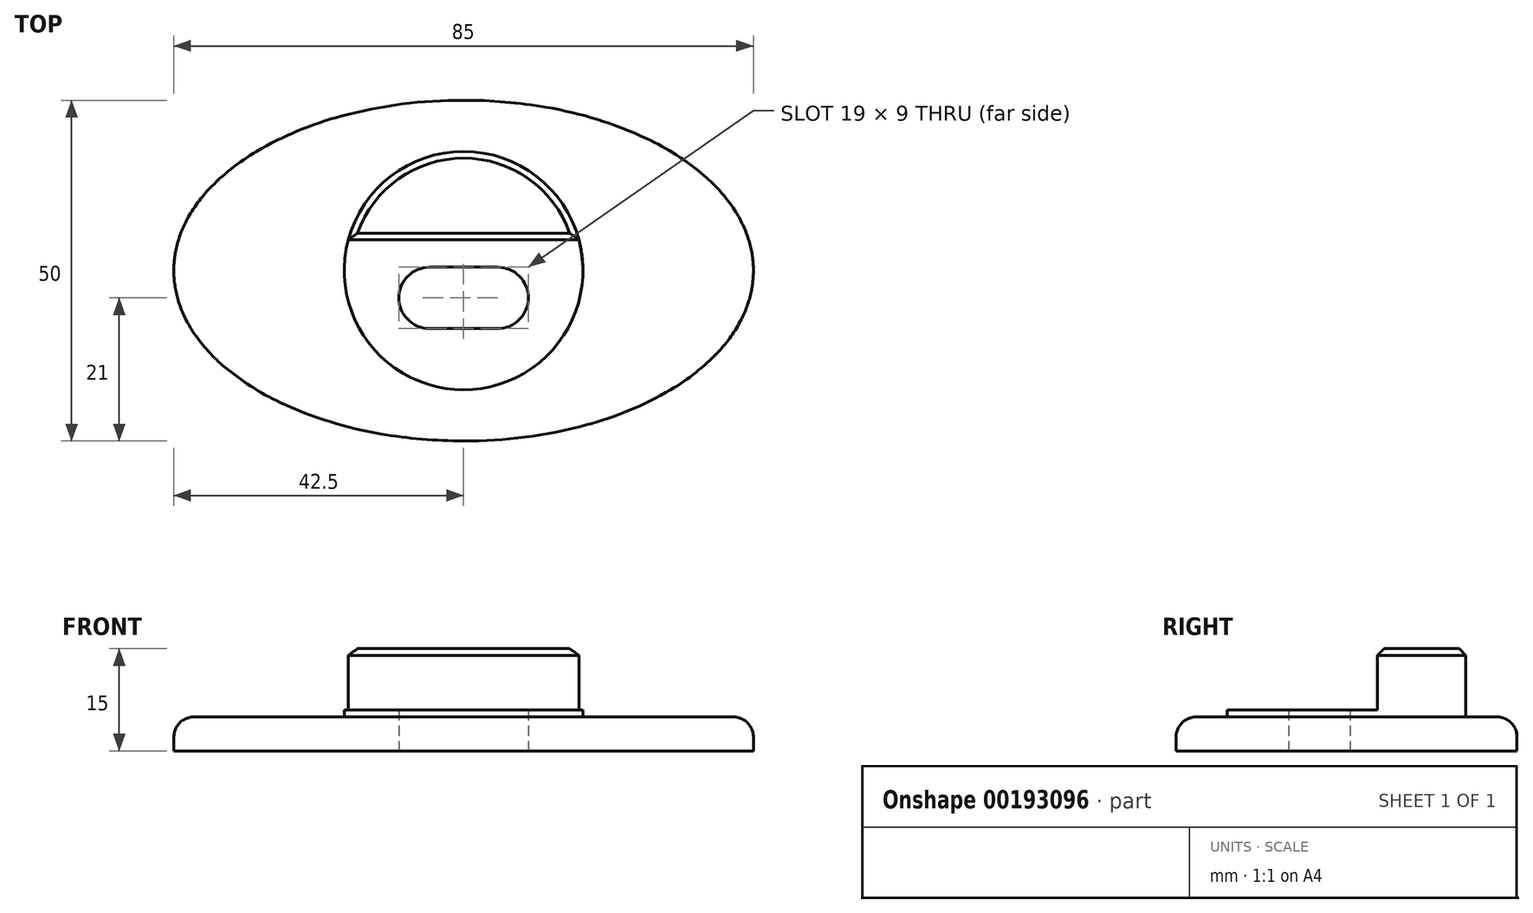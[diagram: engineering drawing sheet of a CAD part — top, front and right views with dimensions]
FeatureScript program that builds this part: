
annotation { "Feature Type Name" : "Feature", "Feature Type Description" : "" }
export const myFeature = defineFeature(function(context is Context, id is Id, definition is map)
    precondition{}
    {
        {
            var Q0;
            Q0=qCreatedBy(makeId("Top.planeOp"),FACE);
            var sketch = newSketch(context, id + "F0", { "sketchPlane" : qUnion([Q0])});
            skArc(sketch, "E0", {"start": v(0, 25) * mm, "mid": v(-9.05, 24.44) * mm, "end": v(-17.95, 22.67) * mm});
            skArc(sketch, "E1", {"start": v(-17.95, 22.67) * mm, "mid": v(-24.33, 20.5) * mm, "end": v(-30.36, 17.5) * mm});
            skArc(sketch, "E2", {"start": v(-30.36, 17.5) * mm, "mid": v(-34.05, 14.96) * mm, "end": v(-37.35, 11.94) * mm});
            skArc(sketch, "E3", {"start": v(-37.35, 11.94) * mm, "mid": v(-39.21, 9.66) * mm, "end": v(-40.74, 7.15) * mm});
            skArc(sketch, "E4", {"start": v(-40.74, 7.15) * mm, "mid": v(-41.66, 4.99) * mm, "end": v(-42.26, 2.72) * mm});
            skArc(sketch, "E5", {"start": v(-42.26, 2.72) * mm, "mid": v(-42.44, 1.37) * mm, "end": v(-42.5, 0) * mm});
            skArc(sketch, "E6", {"start": v(-42.5, 0) * mm, "mid": v(-42.34, -2.18) * mm, "end": v(-41.87, -4.31) * mm});
            skArc(sketch, "E7", {"start": v(-41.87, -4.31) * mm, "mid": v(-40.97, -6.67) * mm, "end": v(-39.75, -8.88) * mm});
            skArc(sketch, "E8", {"start": v(-39.75, -8.88) * mm, "mid": v(-37.7, -11.56) * mm, "end": v(-35.3, -13.92) * mm});
            skArc(sketch, "E9", {"start": v(-35.3, -13.92) * mm, "mid": v(-31.25, -16.94) * mm, "end": v(-26.82, -19.4) * mm});
            skArc(sketch, "E10", {"start": v(-26.82, -19.4) * mm, "mid": v(-19.64, -22.18) * mm, "end": v(-12.15, -23.97) * mm});
            skArc(sketch, "E11", {"start": v(-12.15, -23.97) * mm, "mid": v(-6.1, -24.75) * mm, "end": v(0, -25) * mm});
            skArc(sketch, "E12", {"start": v(0, -25) * mm, "mid": v(9.05, -24.44) * mm, "end": v(17.95, -22.67) * mm});
            skArc(sketch, "E13", {"start": v(17.95, -22.67) * mm, "mid": v(24.33, -20.5) * mm, "end": v(30.36, -17.5) * mm});
            skArc(sketch, "E14", {"start": v(30.36, -17.5) * mm, "mid": v(34.05, -14.96) * mm, "end": v(37.35, -11.94) * mm});
            skArc(sketch, "E15", {"start": v(37.35, -11.94) * mm, "mid": v(39.21, -9.66) * mm, "end": v(40.74, -7.15) * mm});
            skArc(sketch, "E16", {"start": v(40.74, -7.15) * mm, "mid": v(41.66, -4.99) * mm, "end": v(42.26, -2.72) * mm});
            skArc(sketch, "E17", {"start": v(42.26, -2.72) * mm, "mid": v(42.44, -1.37) * mm, "end": v(42.5, 0) * mm});
            skArc(sketch, "E18", {"start": v(42.5, 0) * mm, "mid": v(42.34, 2.18) * mm, "end": v(41.87, 4.31) * mm});
            skArc(sketch, "E19", {"start": v(41.87, 4.31) * mm, "mid": v(40.97, 6.67) * mm, "end": v(39.75, 8.88) * mm});
            skArc(sketch, "E20", {"start": v(39.75, 8.88) * mm, "mid": v(37.7, 11.56) * mm, "end": v(35.3, 13.92) * mm});
            skArc(sketch, "E21", {"start": v(35.3, 13.92) * mm, "mid": v(31.25, 16.94) * mm, "end": v(26.82, 19.4) * mm});
            skArc(sketch, "E22", {"start": v(26.82, 19.4) * mm, "mid": v(19.64, 22.18) * mm, "end": v(12.15, 23.97) * mm});
            skArc(sketch, "E23", {"start": v(12.15, 23.97) * mm, "mid": v(6.1, 24.75) * mm, "end": v(0, 25) * mm});
            skLineSegment(sketch, "E24", {"start": v(-16.91, 4.5) * mm, "end": v(16.91, 4.5) * mm});
            skCircle(sketch, "E25", {"center": v(0, 0) * mm, "radius": 17.5 * mm});
            skArc(sketch, "E26", {"start": v(-5, -1.5) * mm, "mid": v(-7.5, -4) * mm, "end": v(-5, -6.5) * mm});
            skLineSegment(sketch, "E27", {"start": v(-5, -6.5) * mm, "end": v(5, -6.5) * mm});
            skArc(sketch, "E28", {"start": v(5, -6.5) * mm, "mid": v(7.5, -4) * mm, "end": v(5, -1.5) * mm});
            skLineSegment(sketch, "E29", {"start": v(5, -1.5) * mm, "end": v(-5, -1.5) * mm});
            skArc(sketch, "E30", {"start": v(-5, 0.5) * mm, "mid": v(-9.5, -4) * mm, "end": v(-5, -8.5) * mm});
            skLineSegment(sketch, "E31", {"start": v(-5, -8.5) * mm, "end": v(5, -8.5) * mm});
            skArc(sketch, "E32", {"start": v(5, -8.5) * mm, "mid": v(9.5, -4) * mm, "end": v(5, 0.5) * mm});
            skLineSegment(sketch, "E33", {"start": v(5, 0.5) * mm, "end": v(-5, 0.5) * mm});
            skSolve(sketch);
        }
        {
            var Q0;
            {var subQ0=sQuery(id+"F0.wireOp",EDGE,"E24");Q0=makeQuery(id+"F0.imprint","IMPRINT",FACE,{"disambiguationData":[TD([[makeQuery(id+"F0.imprint","IMPRINT",EDGE,{"derivedFrom":subQ0}),1.0]])]});}
            extrude(context, id + "F1", {"entities" : qUnion([Q0]), "depth" : 10 * mm});
        }
        {
            var Q0;
            {var subQ0=sQuery(id+"F0.wireOp",EDGE,"E24");Q0=makeQuery(id+"F0.imprint","IMPRINT",FACE,{"disambiguationData":[TD([[makeQuery(id+"F0.imprint","IMPRINT",EDGE,{"derivedFrom":subQ0}),-1.0]])]});}
            extrude(context, id + "F2", {"entities" : qUnion([Q0]), "operationType" : NewBodyOperationType.ADD, "depth" : 1 * mm});
        }
        {
            var Q0;
            Q0=makeQuery(id+"F0.imprint","IMPRINT",FACE,{"disambiguationData":[TD([[makeQuery(id+"F0.imprint","IMPRINT",EDGE,{"derivedFrom":sQuery(id+"F0.wireOp",EDGE,"E0")}),1.0]])]});
            var Q1;
            Q1=makeQuery(id+"F1.opExtrude","CAP_FACE",FACE,{"disambiguationData":[OSD([sQuery(id+"F0.wireOp",EDGE,"E24"),sQuery(id+"F0.wireOp",EDGE,"E25")])],"isStart":false});
            var Q2;
            Q2=makeQuery(id+"F2.opExtrude","CAP_FACE",FACE,{"disambiguationData":[OSD([sQuery(id+"F0.wireOp",EDGE,"E24"),sQuery(id+"F0.wireOp",EDGE,"E25"),sQuery(id+"F0.wireOp",EDGE,"E30"),sQuery(id+"F0.wireOp",EDGE,"E31"),sQuery(id+"F0.wireOp",EDGE,"E32"),sQuery(id+"F0.wireOp",EDGE,"E33")])],"isStart":false});
            extrude(context, id + "F3", {"entities" : qUnion([Q0, Q1, Q2]), "operationType" : NewBodyOperationType.ADD, "depth" : 5 * mm});
        }
        {
            var Q0;
            Q0=makeQuery(id+"F3.opExtrude","CAP_EDGE",EDGE,{"disambiguationData":[OSD([sQuery(id+"F0.wireOp",EDGE,"E10")])],"isStart":false});
            var Q1;
            Q1=makeQuery(id+"F3.opExtrude","CAP_EDGE",EDGE,{"disambiguationData":[OSD([sQuery(id+"F0.wireOp",EDGE,"E23")])],"isStart":false});
            var Q2;
            Q2=makeQuery(id+"F3.opExtrude","CAP_EDGE",EDGE,{"disambiguationData":[OSD([sQuery(id+"F0.wireOp",EDGE,"E0")])],"isStart":false});
            var Q3;
            Q3=makeQuery(id+"F3.opExtrude","CAP_EDGE",EDGE,{"disambiguationData":[OSD([sQuery(id+"F0.wireOp",EDGE,"E1")])],"isStart":false});
            var Q4;
            Q4=makeQuery(id+"F3.opExtrude","CAP_EDGE",EDGE,{"disambiguationData":[OSD([sQuery(id+"F0.wireOp",EDGE,"E2")])],"isStart":false});
            var Q5;
            Q5=makeQuery(id+"F3.opExtrude","CAP_EDGE",EDGE,{"disambiguationData":[OSD([sQuery(id+"F0.wireOp",EDGE,"E3")])],"isStart":false});
            var Q6;
            Q6=makeQuery(id+"F3.opExtrude","CAP_EDGE",EDGE,{"disambiguationData":[OSD([sQuery(id+"F0.wireOp",EDGE,"E22")])],"isStart":false});
            var Q7;
            Q7=makeQuery(id+"F3.opExtrude","CAP_EDGE",EDGE,{"disambiguationData":[OSD([sQuery(id+"F0.wireOp",EDGE,"E21")])],"isStart":false});
            var Q8;
            Q8=makeQuery(id+"F3.opExtrude","CAP_EDGE",EDGE,{"disambiguationData":[OSD([sQuery(id+"F0.wireOp",EDGE,"E20")])],"isStart":false});
            var Q9;
            Q9=makeQuery(id+"F3.opExtrude","CAP_EDGE",EDGE,{"disambiguationData":[OSD([sQuery(id+"F0.wireOp",EDGE,"E18")])],"isStart":false});
            var Q10;
            Q10=makeQuery(id+"F3.opExtrude","CAP_EDGE",EDGE,{"disambiguationData":[OSD([sQuery(id+"F0.wireOp",EDGE,"E4")])],"isStart":false});
            var Q11;
            Q11=makeQuery(id+"F3.opExtrude","CAP_EDGE",EDGE,{"disambiguationData":[OSD([sQuery(id+"F0.wireOp",EDGE,"E6")])],"isStart":false});
            var Q12;
            Q12=makeQuery(id+"F3.opExtrude","CAP_EDGE",EDGE,{"disambiguationData":[OSD([sQuery(id+"F0.wireOp",EDGE,"E5")])],"isStart":false});
            var Q13;
            Q13=makeQuery(id+"F3.opExtrude","CAP_EDGE",EDGE,{"disambiguationData":[OSD([sQuery(id+"F0.wireOp",EDGE,"E7")])],"isStart":false});
            var Q14;
            Q14=makeQuery(id+"F3.opExtrude","CAP_EDGE",EDGE,{"disambiguationData":[OSD([sQuery(id+"F0.wireOp",EDGE,"E8")])],"isStart":false});
            var Q15;
            Q15=makeQuery(id+"F3.opExtrude","CAP_EDGE",EDGE,{"disambiguationData":[OSD([sQuery(id+"F0.wireOp",EDGE,"E9")])],"isStart":false});
            var Q16;
            Q16=makeQuery(id+"F3.opExtrude","CAP_EDGE",EDGE,{"disambiguationData":[OSD([sQuery(id+"F0.wireOp",EDGE,"E11")])],"isStart":false});
            var Q17;
            Q17=makeQuery(id+"F3.opExtrude","CAP_EDGE",EDGE,{"disambiguationData":[OSD([sQuery(id+"F0.wireOp",EDGE,"E12")])],"isStart":false});
            var Q18;
            Q18=makeQuery(id+"F3.opExtrude","CAP_EDGE",EDGE,{"disambiguationData":[OSD([sQuery(id+"F0.wireOp",EDGE,"E13")])],"isStart":false});
            var Q19;
            Q19=makeQuery(id+"F3.opExtrude","CAP_EDGE",EDGE,{"disambiguationData":[OSD([sQuery(id+"F0.wireOp",EDGE,"E14")])],"isStart":false});
            var Q20;
            Q20=makeQuery(id+"F3.opExtrude","CAP_EDGE",EDGE,{"disambiguationData":[OSD([sQuery(id+"F0.wireOp",EDGE,"E19")])],"isStart":false});
            var Q21;
            Q21=makeQuery(id+"F3.opExtrude","CAP_EDGE",EDGE,{"disambiguationData":[OSD([sQuery(id+"F0.wireOp",EDGE,"E17")])],"isStart":false});
            var Q22;
            Q22=makeQuery(id+"F3.opExtrude","CAP_EDGE",EDGE,{"disambiguationData":[OSD([sQuery(id+"F0.wireOp",EDGE,"E16")])],"isStart":false});
            var Q23;
            Q23=makeQuery(id+"F3.opExtrude","CAP_EDGE",EDGE,{"disambiguationData":[OSD([sQuery(id+"F0.wireOp",EDGE,"E15")])],"isStart":false});
            fillet(context, id + "F4", {"entities" : qUnion([Q0, Q1, Q2, Q3, Q4, Q5, Q6, Q7, Q8, Q9, Q10, Q11, Q12, Q13, Q14, Q15, Q16, Q17, Q18, Q19, Q20, Q21, Q22, Q23]), "radius" : 3 * mm, "tangentPropagation" : true, "allowEdgeOverflow" : false});
        }
        {
            var Q0;
            Q0=makeQuery(id+"F3.opExtrude","CAP_FACE",FACE,{"disambiguationData":[OSD([sQuery(id+"F0.wireOp",EDGE,"E24"),sQuery(id+"F0.wireOp",EDGE,"E25")])],"isStart":false});
            chamfer(context, id + "F5", {"entities" : qUnion([Q0]), "width" : 1 * mm, "tangentPropagation" : true});
        }
    });
